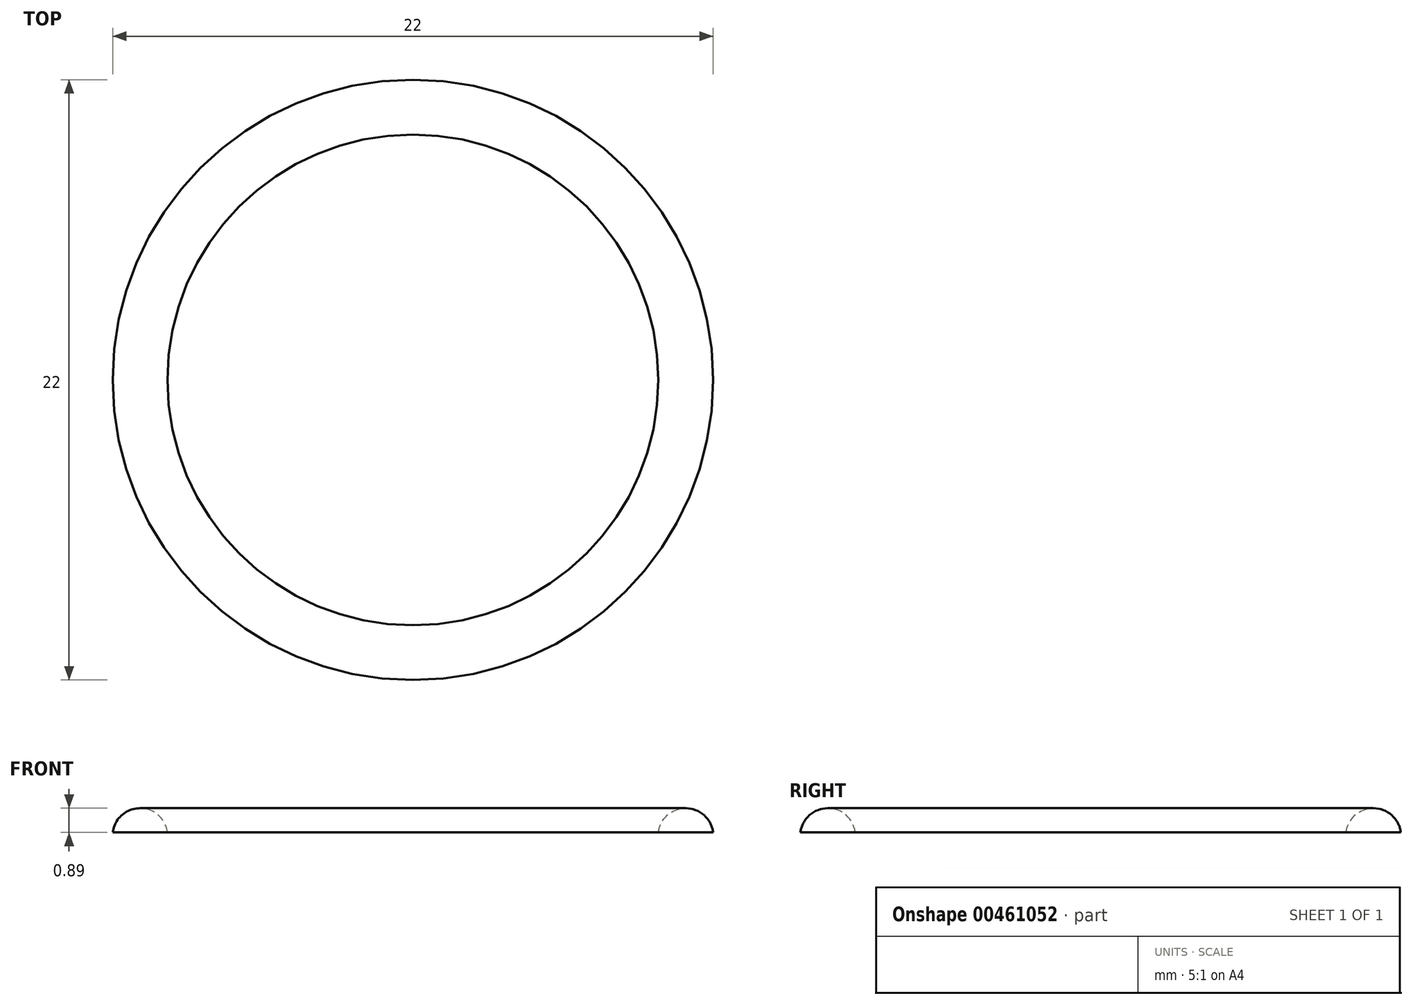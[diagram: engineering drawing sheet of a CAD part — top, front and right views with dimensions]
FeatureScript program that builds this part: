
annotation { "Feature Type Name" : "Feature", "Feature Type Description" : "" }
export const myFeature = defineFeature(function(context is Context, id is Id, definition is map)
    precondition{}
    {
        {
            var Q0;
            Q0=qCreatedBy(makeId("Front.planeOp"),FACE);
            var sketch = newSketch(context, id + "F0", { "sketchPlane" : qUnion([Q0])});
            skLineSegment(sketch, "E0.bottom", {"start": v(0, 0) * mm, "end": v(11, 0) * mm});
            skLineSegment(sketch, "E0.top", {"start": v(0, 25) * mm, "end": v(11, 25) * mm});
            skLineSegment(sketch, "E0.left", {"start": v(0, 0) * mm, "end": v(0, 25) * mm});
            skLineSegment(sketch, "E0.right", {"start": v(11, 0) * mm, "end": v(11, 25) * mm});
            skLineSegment(sketch, "E1.bottom", {"start": v(0, 0) * mm, "end": v(9, 0) * mm});
            skLineSegment(sketch, "E2", {"start": v(9, 0) * mm, "end": v(11, 25) * mm});
            skPoint(sketch, "E3.visualSharp", {"position": v(9, 0) * mm});
            skLineSegment(sketch, "E4.0", {"start": v(7.52, 6.6) * mm, "end": v(9, 25) * mm});
            skLineSegment(sketch, "E4.1", {"start": v(0, 2) * mm, "end": v(2.54, 2) * mm});
            skPoint(sketch, "E5.visualSharp", {"position": v(7.15, 2) * mm});
            skArc(sketch, "E5.filletArc", {"start": v(2.54, 2) * mm, "mid": v(5.93, 3.33) * mm, "end": v(7.52, 6.6) * mm});
            skArc(sketch, "E6", {"start": v(10.97, 24.6) * mm, "mid": v(10.16, 25.88) * mm, "end": v(8.99, 24.92) * mm});
            skPoint(sketch, "E6.third.point", {"position": v(9.92, 23.87) * mm});
            skSolve(sketch);
        }
        {
            var Q0;
            {var subQ0=sQuery(id+"F0.wireOp",EDGE,"E1.bottom");Q0=makeQuery(id+"F0.imprint","IMPRINT",FACE,{"disambiguationData":[TD([[makeQuery(id+"F0.imprint","IMPRINT",EDGE,{"derivedFrom":subQ0}),1.0]])]});}
            var Q1;
            {var subQ0=sQuery(id+"F0.wireOp",EDGE,"E6");var subQ1=sQuery(id+"F0.wireOp",EDGE,"E0.top");var subQ3=makeQuery(id+"F0.imprint","INTERSECT",VERTEX,{"derivedFrom":[subQ1,sQuery(id+"F0.wireOp",EDGE,"E4.0"),subQ0]});Q1=makeQuery(id+"F0.imprint","IMPRINT",FACE,{"disambiguationData":[TD([[makeQuery(id+"F0.imprint","IMPRINT",EDGE,{"disambiguationData":[TD([[subQ3,-1.0]])],"derivedFrom":subQ1}),1.0]])]});}
            var Q2;
            Q2=sQuery(id+"F0.wireOp",EDGE,"E0.left");
            revolve(context, id + "F1", {"entities" : qUnion([Q0, Q1]), "axis" : qUnion([Q2]), "revolveType" : RevolveType.FULL});
        }
    });
